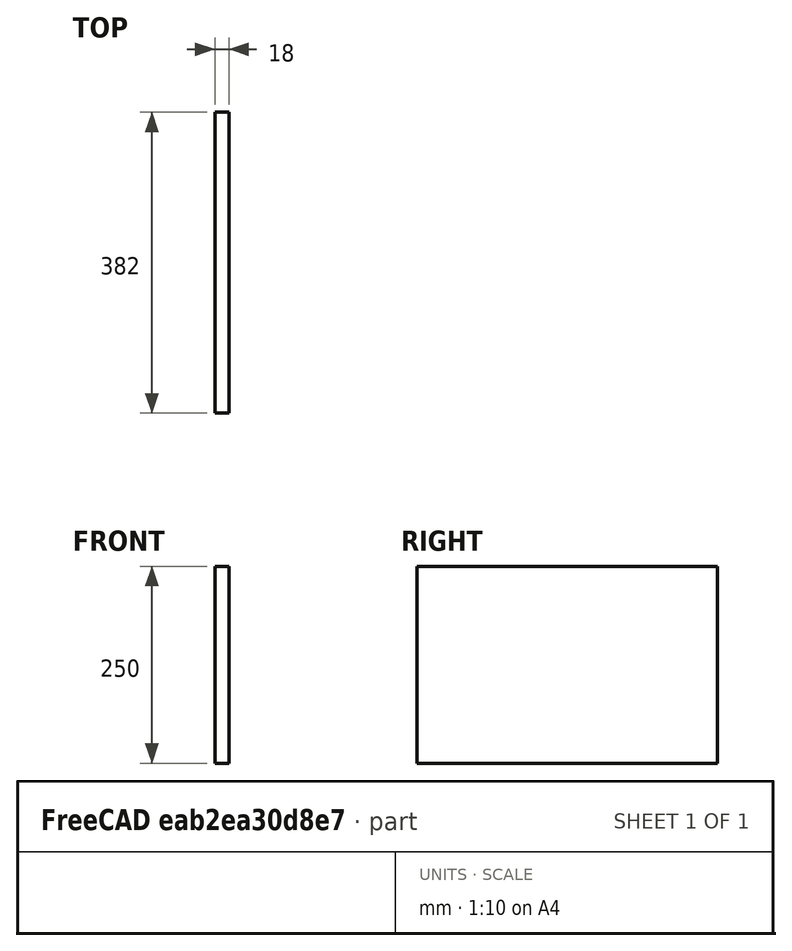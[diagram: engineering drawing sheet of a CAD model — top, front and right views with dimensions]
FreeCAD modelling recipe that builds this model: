
FCSTD DOCUMENT  (FreeCAD 0.18R4 (GitTag))
Label: divider
License: All rights reserved
LicenseURL: http://en.wikipedia.org/wiki/All_rights_reserved
objects: Sketcher::SketchObject×1, PartDesign::Pad×1, PartDesign::Body×1
note: 4 computed .brp shape members not serialized (recipe doc carries the construction recipe); baked Part::Feature solids carry a one-line shape summary decoded from their .brp

FEATURE [Sketcher::SketchObject] Sketch
  MapMode = 5
  Placement = pos=(0,0,0) rot=(0.57735,0.57735,0.57735;2.0944rad)
  Support = -> [YZ_Plane]
  sketch-geometry (4):
    g0: LineSegment StartX=0 StartY=0 StartZ=0 EndX=-382 EndY=0 EndZ=0
    g1: LineSegment StartX=-382 StartY=0 StartZ=0 EndX=-382 EndY=250 EndZ=0
    g2: LineSegment StartX=-382 StartY=250 StartZ=0 EndX=0 EndY=250 EndZ=0
    g3: LineSegment StartX=0 StartY=250 StartZ=0 EndX=0 EndY=0 EndZ=0
  constraints (11):
    c: Coincident(g0,g1)
    c: Coincident(g1,g2)
    c: Coincident(g2,g3)
    c: Coincident(g3,g0)
    c: Horizontal(g0)
    c: Horizontal(g2)
    c: Vertical(g1)
    c: Vertical(g3)
    c: Coincident(g0,g-1)
    c: DistanceY(g3,g3) = 250
    c: DistanceX(g0,g0) = 382
FEATURE [PartDesign::Pad] Pad
  Length = 18
  Length2 = 100
  Placement = pos=(0,0,0) rot=(0.57735,0.57735,0.57735;2.0944rad)
  Profile = -> Sketch
  Type = 0
FEATURE [PartDesign::Body] Body
  Group = -> [Sketch,Pad]
  Origin = -> Origin
  Tip = -> Pad
